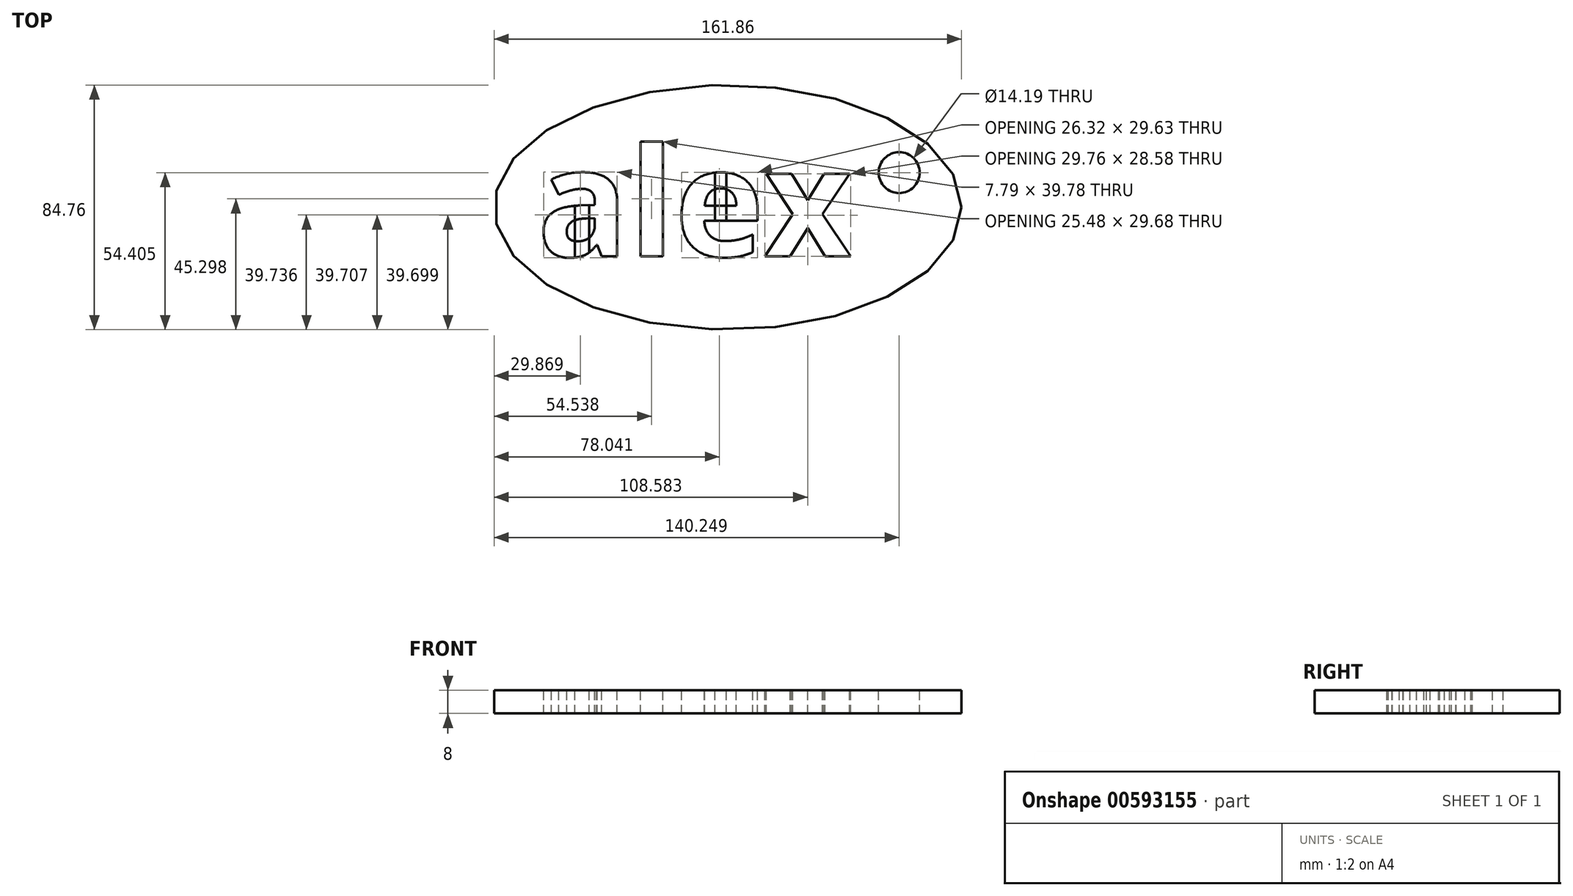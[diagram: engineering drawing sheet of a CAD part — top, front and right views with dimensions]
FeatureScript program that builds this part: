
annotation { "Feature Type Name" : "Feature", "Feature Type Description" : "" }
export const myFeature = defineFeature(function(context is Context, id is Id, definition is map)
    precondition{}
    {
        {
            var Q0;
            Q0=qCreatedBy(makeId("Top.planeOp"),FACE);
            var sketch = newSketch(context, id + "F0", { "sketchPlane" : qUnion([Q0])});
            skEllipse(sketch, "E0", {"center": v(-29.83, 0) * mm, "majorRadius": 80.93 * mm, "minorRadius": 42.38 * mm, "majorAxis": v(1, 0)});
            skSolve(sketch);
        }
        {
            var Q0;
            Q0 = qSketchRegion(id + "F0", true);
            extrude(context, id + "F1", {"entities" : qUnion([Q0]), "depth" : 8 * mm, "offsetDistance" : 25 * mm});
        }
        {
            var Q0;
            Q0=makeQuery(id+"F1.opExtrude","CAP_FACE",FACE,{"disambiguationData":[OSD([sQuery(id+"F0.wireOp",EDGE,"E0")])],"isStart":false});
            var sketch = newSketch(context, id + "F2", { "sketchPlane" : qUnion([Q0])});
            skText(sketch, "E1", { "text": "alex", "fontName": "OpenSans-Bold.ttf"});
            skCircle(sketch, "E2", {"center": v(29.49, 12.03) * mm, "radius": 7.1 * mm});
            const initialGuessF2  = {"E1": [-0.09583, -0.01697, 1, 0, 0.03769]};
            skSetInitialGuess(sketch, initialGuessF2);
            skSolve(sketch);
        }
        {
            var Q0;
            Q0=makeQuery(id+"F2.imprint","IMPRINT",FACE,{"disambiguationData":[TD([[makeQuery(id+"F2.imprint","IMPRINT",EDGE,{"derivedFrom":sQuery(id+"F2.wireOp",EDGE,"E1.sketch_text.stroke-25")}),-1.0]])]});
            var Q1;
            Q1=makeQuery(id+"F2.imprint","IMPRINT",FACE,{"disambiguationData":[TD([[makeQuery(id+"F2.imprint","IMPRINT",EDGE,{"derivedFrom":sQuery(id+"F2.wireOp",EDGE,"E1.sketch_text.stroke-49")}),-1.0]])]});
            var Q2;
            Q2=makeQuery(id+"F2.imprint","IMPRINT",FACE,{"disambiguationData":[TD([[makeQuery(id+"F2.imprint","IMPRINT",EDGE,{"derivedFrom":sQuery(id+"F2.wireOp",EDGE,"E2")}),1.0]])]});
            var Q3;
            Q3=makeQuery(id+"F2.imprint","IMPRINT",FACE,{"disambiguationData":[TD([[makeQuery(id+"F2.imprint","IMPRINT",EDGE,{"derivedFrom":sQuery(id+"F2.wireOp",EDGE,"E1.sketch_text.stroke-29")}),-1.0]])]});
            var Q4;
            Q4=makeQuery(id+"F2.imprint","IMPRINT",FACE,{"disambiguationData":[TD([[makeQuery(id+"F2.imprint","IMPRINT",EDGE,{"derivedFrom":sQuery(id+"F2.wireOp",EDGE,"E1.sketch_text.stroke-0")}),-1.0]])]});
            extrude(context, id + "F3", {"entities" : qUnion([Q0, Q1, Q2, Q3, Q4]), "operationType" : NewBodyOperationType.REMOVE, "oppositeDirection" : true, "depth" : 25 * mm, "offsetDistance" : 25 * mm});
        }
        {
            var Q0;
            {var subQ0=sQuery(id+"F0.wireOp",EDGE,"E0");Q0=makeQuery(id+"F3.boolean.opBoolean","SPLIT",FACE,{"disambiguationData":[TD([makeQuery(id+"F1.opExtrude","SWEPT_FACE",FACE,{"disambiguationData":[OSD([subQ0])]})])],"derivedFrom":makeQuery(id+"F1.opExtrude","CAP_FACE",FACE,{"disambiguationData":[OSD([subQ0])],"isStart":false})});}
            var sketch = newSketch(context, id + "F4", { "sketchPlane" : qUnion([Q0])});
            skLineSegment(sketch, "E3.bottom", {"start": v(-82.84, 3.23) * mm, "end": v(-77.86, 3.23) * mm});
            skLineSegment(sketch, "E3.top", {"start": v(-82.84, -20.82) * mm, "end": v(-77.86, -20.82) * mm});
            skLineSegment(sketch, "E3.left", {"start": v(-82.84, 3.23) * mm, "end": v(-82.84, -20.82) * mm});
            skLineSegment(sketch, "E3.right", {"start": v(-77.86, 3.23) * mm, "end": v(-77.86, -20.82) * mm});
            skPoint(sketch, "E4.oppositeSnap0", {"position": v(-28.77, -4.62) * mm});
            skLineSegment(sketch, "E4.bottom", {"start": v(-34.33, 16.38) * mm, "end": v(-28.77, 16.38) * mm});
            skLineSegment(sketch, "E4.top", {"start": v(-34.33, -7.7) * mm, "end": v(-28.77, -7.7) * mm});
            skLineSegment(sketch, "E4.left", {"start": v(-34.33, 16.38) * mm, "end": v(-34.33, -7.7) * mm});
            skLineSegment(sketch, "E4.right", {"start": v(-28.77, 16.38) * mm, "end": v(-28.77, -7.7) * mm});
            skLineSegment(sketch, "E5", {"start": v(-30.29, 16.38) * mm, "end": v(-30.29, -7.7) * mm});
            skSolve(sketch);
        }
        {
            var Q0;
            {var subQ1=makeQuery(id+"F3.boolean.opBoolean","COPY",EDGE,{"derivedFrom":makeQuery(id+"F3.opExtrude","CAP_EDGE",EDGE,{"disambiguationData":[OSD([sQuery(id+"F2.wireOp",EDGE,"E1.sketch_text.stroke-37")])],"isStart":true})});var subQ5=sQuery(id+"F4.wireOp",EDGE,"E4.left");var subQ6=makeQuery(id+"F4.imprint","INTERSECT",VERTEX,{"derivedFrom":[subQ1,subQ5]});Q0=makeQuery(id+"F4.imprint","IMPRINT",FACE,{"disambiguationData":[TD([[makeQuery(id+"F4.imprint","IMPRINT",EDGE,{"disambiguationData":[TD([[subQ6,-1.0]])],"derivedFrom":subQ5}),1.0]])]});}
            var Q1;
            {var subQ3=sQuery(id+"F4.wireOp",EDGE,"E3.left");var subQ9=makeQuery(id+"F3.boolean.opBoolean","COPY",EDGE,{"derivedFrom":makeQuery(id+"F3.opExtrude","CAP_EDGE",EDGE,{"disambiguationData":[OSD([sQuery(id+"F2.wireOp",EDGE,"E1.sketch_text.stroke-7")])],"isStart":true})});var subQ10=makeQuery(id+"F4.imprint","INTERSECT",VERTEX,{"derivedFrom":[subQ9,subQ3]});Q1=makeQuery(id+"F4.imprint","IMPRINT",FACE,{"disambiguationData":[TD([[makeQuery(id+"F4.imprint","IMPRINT",EDGE,{"disambiguationData":[TD([[subQ10,-1.0]])],"derivedFrom":subQ3}),1.0]])]});}
            var Q2;
            {var subQ0=sQuery(id+"F0.wireOp",EDGE,"E0");Q2=makeQuery(id+"F3.boolean.opBoolean","SPLIT",FACE,{"disambiguationData":[TD([makeQuery(id+"F1.opExtrude","SWEPT_FACE",FACE,{"disambiguationData":[OSD([subQ0])]})])],"derivedFrom":makeQuery(id+"F1.opExtrude","CAP_FACE",FACE,{"disambiguationData":[OSD([subQ0])],"isStart":true})});}
            extrude(context, id + "F5", {"entities" : qUnion([Q0, Q1]), "endBound" : BoundingType.UP_TO_SURFACE, "oppositeDirection" : true, "depth" : 25 * mm, "endBoundEntityFace" : qUnion([Q2]), "offsetDistance" : 25 * mm});
        }
    });
